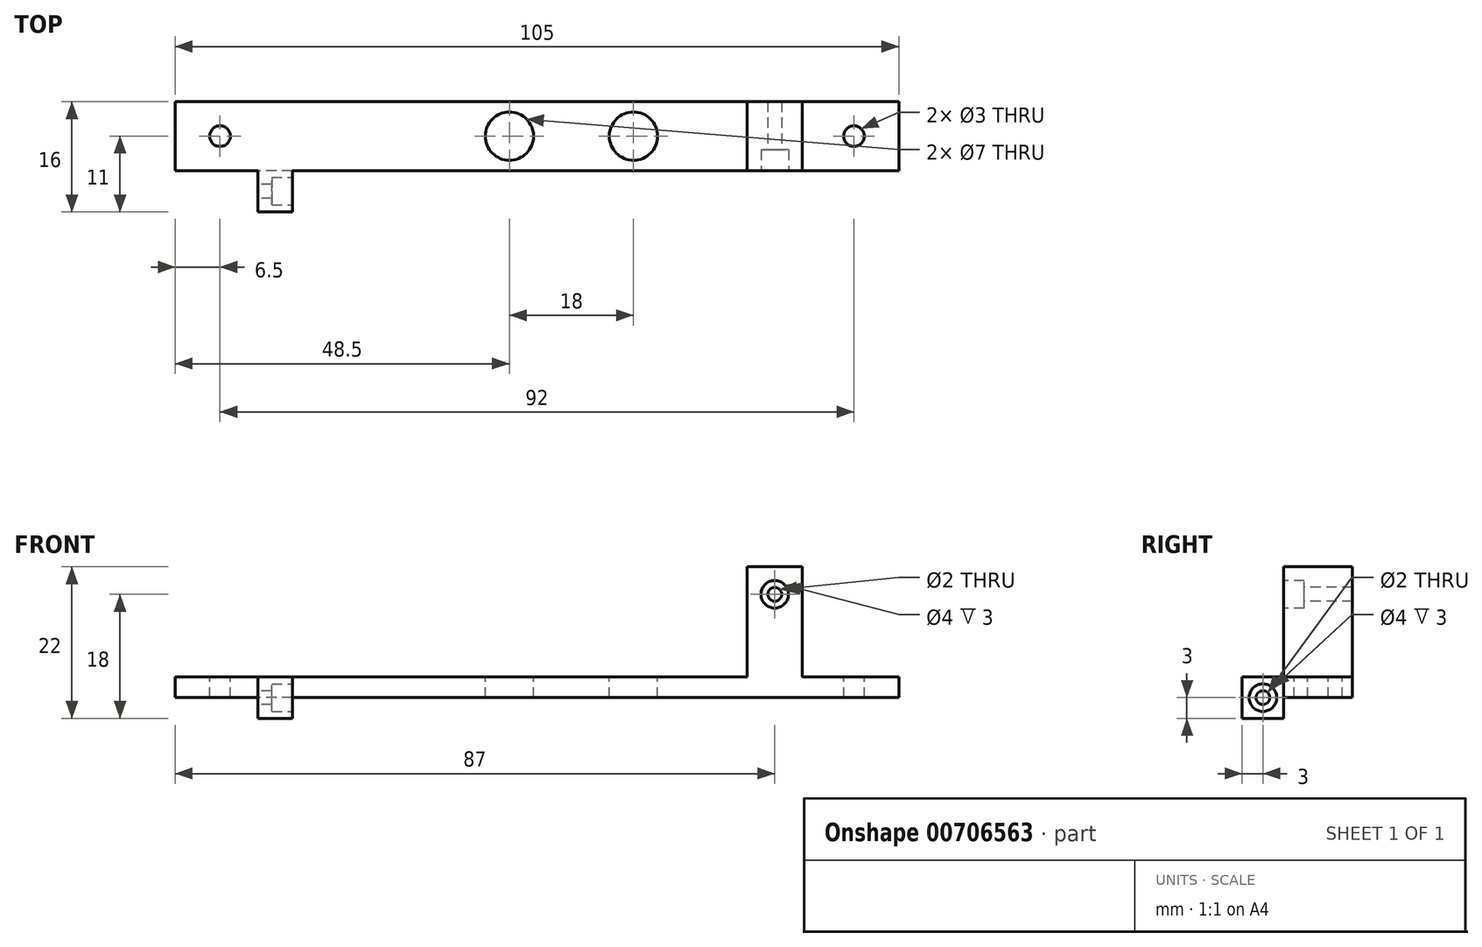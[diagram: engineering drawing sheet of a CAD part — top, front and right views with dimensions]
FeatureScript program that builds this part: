
annotation { "Feature Type Name" : "Feature", "Feature Type Description" : "" }
export const myFeature = defineFeature(function(context is Context, id is Id, definition is map)
    precondition{}
    {
        {
            var Q0;
            Q0=qCreatedBy(makeId("Top.planeOp"),FACE);
            var sketch = newSketch(context, id + "F0", { "sketchPlane" : qUnion([Q0])});
            skLineSegment(sketch, "E0.bottom", {"start": v(52.5, -5) * mm, "end": v(-52.5, -5) * mm});
            skLineSegment(sketch, "E0.top", {"start": v(52.5, 5) * mm, "end": v(-52.5, 5) * mm});
            skLineSegment(sketch, "E0.left", {"start": v(52.5, -5) * mm, "end": v(52.5, 5) * mm});
            skLineSegment(sketch, "E0.right", {"start": v(-52.5, -5) * mm, "end": v(-52.5, 5) * mm});
            skPoint(sketch, "E0.middle", {"position": v(0, 0) * mm});
            skLineSegment(sketch, "E1", {"start": v(-52.5, 0) * mm, "end": v(52.5, 0) * mm});
            skPoint(sketch, "E2", {"position": v(-46, 0) * mm});
            skPoint(sketch, "E3", {"position": v(46, 0) * mm});
            skSolve(sketch);
        }
        {
            var Q0;
            Q0 = qSketchRegion(id + "F0", true);
            extrude(context, id + "F1", {"entities" : qUnion([Q0]), "depth" : 3 * mm, "offsetDistance" : 25 * mm});
        }
        {
            var Q0;
            Q0=makeQuery(id+"F1.opExtrude","CAP_FACE",FACE,{"disambiguationData":[OSD([sQuery(id+"F0.wireOp",EDGE,"E0.bottom"),sQuery(id+"F0.wireOp",EDGE,"E0.top"),sQuery(id+"F0.wireOp",EDGE,"E0.left"),sQuery(id+"F0.wireOp",EDGE,"E0.right")])],"isStart":false});
            var sketch = newSketch(context, id + "F2", { "sketchPlane" : qUnion([Q0])});
            skLineSegment(sketch, "E4", {"start": v(-52.5, 0) * mm, "end": v(52.5, 0) * mm});
            skPoint(sketch, "E5", {"position": v(-46, 0) * mm});
            skPoint(sketch, "E6", {"position": v(46, 0) * mm});
            skCircle(sketch, "E7", {"center": v(-46, 0) * mm, "radius": 1.5 * mm});
            skCircle(sketch, "E8", {"center": v(46, 0) * mm, "radius": 1.5 * mm});
            skSolve(sketch);
        }
        {
            var Q0;
            Q0 = qSketchRegion(id + "F2", true);
            extrude(context, id + "F3", {"entities" : qUnion([Q0]), "operationType" : NewBodyOperationType.REMOVE, "endBound" : BoundingType.THROUGH_ALL, "oppositeDirection" : true, "depth" : 25 * mm, "offsetDistance" : 25 * mm});
        }
        {
            var Q0;
            Q0=makeQuery(id+"F1.opExtrude","CAP_FACE",FACE,{"disambiguationData":[OSD([sQuery(id+"F0.wireOp",EDGE,"E0.bottom"),sQuery(id+"F0.wireOp",EDGE,"E0.top"),sQuery(id+"F0.wireOp",EDGE,"E0.left"),sQuery(id+"F0.wireOp",EDGE,"E0.right")])],"isStart":false});
            var sketch = newSketch(context, id + "F4", { "sketchPlane" : qUnion([Q0])});
            skPoint(sketch, "E9", {"position": v(-4, 0) * mm});
            skPoint(sketch, "E10", {"position": v(14, 0) * mm});
            skPoint(sketch, "E11", {"position": v(-46, 0) * mm});
            skPoint(sketch, "E12", {"position": v(46, 0) * mm});
            skCircle(sketch, "E13", {"center": v(-4, 0) * mm, "radius": 3.5 * mm});
            skCircle(sketch, "E14", {"center": v(14, 0) * mm, "radius": 3.5 * mm});
            skSolve(sketch);
        }
        {
            var Q0;
            Q0 = qSketchRegion(id + "F4", true);
            extrude(context, id + "F5", {"entities" : qUnion([Q0]), "operationType" : NewBodyOperationType.REMOVE, "endBound" : BoundingType.THROUGH_ALL, "oppositeDirection" : true, "depth" : 25 * mm, "offsetDistance" : 25 * mm});
        }
        {
            var Q0;
            Q0 = qSketchRegion(id + "F4", true);
            extrude(context, id + "F6", {"entities" : qUnion([Q0]), "operationType" : NewBodyOperationType.REMOVE, "endBound" : BoundingType.THROUGH_ALL, "oppositeDirection" : true, "depth" : 25 * mm, "offsetDistance" : 25 * mm});
        }
        {
            var Q0;
            Q0=makeQuery(id+"F1.opExtrude","CAP_FACE",FACE,{"disambiguationData":[OSD([sQuery(id+"F0.wireOp",EDGE,"E0.bottom"),sQuery(id+"F0.wireOp",EDGE,"E0.top"),sQuery(id+"F0.wireOp",EDGE,"E0.left"),sQuery(id+"F0.wireOp",EDGE,"E0.right")])],"isStart":false});
            var sketch = newSketch(context, id + "F7", { "sketchPlane" : qUnion([Q0])});
            skPoint(sketch, "E15", {"position": v(38.5, -5) * mm});
            skLineSegment(sketch, "E16.bottom", {"start": v(38.5, -5) * mm, "end": v(30.5, -5) * mm});
            skLineSegment(sketch, "E16.top", {"start": v(38.5, 5) * mm, "end": v(30.5, 5) * mm});
            skLineSegment(sketch, "E16.left", {"start": v(38.5, -5) * mm, "end": v(38.5, 5) * mm});
            skLineSegment(sketch, "E16.right", {"start": v(30.5, -5) * mm, "end": v(30.5, 5) * mm});
            skSolve(sketch);
        }
        {
            var Q0;
            Q0 = qSketchRegion(id + "F7", true);
            extrude(context, id + "F8", {"entities" : qUnion([Q0]), "operationType" : NewBodyOperationType.ADD, "depth" : 16 * mm, "offsetDistance" : 25 * mm});
        }
        {
            var Q0;
            Q0=makeQuery(id+"F8.boolean.opBoolean","MERGE",FACE,{"derivedFrom":[makeQuery(id+"F1.opExtrude","SWEPT_FACE",FACE,{"disambiguationData":[OSD([sQuery(id+"F0.wireOp",EDGE,"E0.bottom")])]}),makeQuery(id+"F8.opExtrude","SWEPT_FACE",FACE,{"disambiguationData":[OSD([sQuery(id+"F7.wireOp",EDGE,"E16.bottom")])]})]});
            var sketch = newSketch(context, id + "F9", { "sketchPlane" : qUnion([Q0])});
            skPoint(sketch, "E17", {"position": v(34.5, 15) * mm});
            skCircle(sketch, "E18", {"center": v(34.5, 15) * mm, "radius": 1 * mm});
            skSolve(sketch);
        }
        {
            var Q0;
            Q0 = qSketchRegion(id + "F9", true);
            extrude(context, id + "F10", {"entities" : qUnion([Q0]), "operationType" : NewBodyOperationType.REMOVE, "endBound" : BoundingType.THROUGH_ALL, "oppositeDirection" : true, "depth" : 25 * mm, "offsetDistance" : 25 * mm});
        }
        {
            var Q0;
            Q0=makeQuery(id+"F8.boolean.opBoolean","MERGE",FACE,{"derivedFrom":[makeQuery(id+"F1.opExtrude","SWEPT_FACE",FACE,{"disambiguationData":[OSD([sQuery(id+"F0.wireOp",EDGE,"E0.bottom")])]}),makeQuery(id+"F8.opExtrude","SWEPT_FACE",FACE,{"disambiguationData":[OSD([sQuery(id+"F7.wireOp",EDGE,"E16.bottom")])]})]});
            var sketch = newSketch(context, id + "F11", { "sketchPlane" : qUnion([Q0])});
            skPoint(sketch, "E19", {"position": v(34.5, 15) * mm});
            skCircle(sketch, "E20", {"center": v(34.5, 15) * mm, "radius": 2 * mm});
            skSolve(sketch);
        }
        {
            var Q0;
            Q0 = qSketchRegion(id + "F11", true);
            extrude(context, id + "F12", {"entities" : qUnion([Q0]), "operationType" : NewBodyOperationType.REMOVE, "oppositeDirection" : true, "depth" : 3 * mm, "offsetDistance" : 25 * mm});
        }
        {
            var Q0;
            {var subQ0=sQuery(id+"F0.wireOp",EDGE,"E0.right");var subQ1=sQuery(id+"F0.wireOp",EDGE,"E0.top");var subQ2=sQuery(id+"F0.wireOp",EDGE,"E0.bottom");Q0=makeQuery(id+"F8.boolean.opBoolean","SPLIT",FACE,{"disambiguationData":[TD([makeQuery(id+"F1.opExtrude","SWEPT_FACE",FACE,{"disambiguationData":[OSD([subQ0])]})])],"derivedFrom":makeQuery(id+"F1.opExtrude","CAP_FACE",FACE,{"disambiguationData":[OSD([subQ2,subQ1,sQuery(id+"F0.wireOp",EDGE,"E0.left"),subQ0])],"isStart":false})});}
            var sketch = newSketch(context, id + "F13", { "sketchPlane" : qUnion([Q0])});
            skPoint(sketch, "E21", {"position": v(-40.5, -5) * mm});
            skLineSegment(sketch, "E22.bottom", {"start": v(-40.5, -5) * mm, "end": v(-35.5, -5) * mm});
            skLineSegment(sketch, "E22.top", {"start": v(-40.5, -11) * mm, "end": v(-35.5, -11) * mm});
            skLineSegment(sketch, "E22.left", {"start": v(-40.5, -5) * mm, "end": v(-40.5, -11) * mm});
            skLineSegment(sketch, "E22.right", {"start": v(-35.5, -5) * mm, "end": v(-35.5, -11) * mm});
            skSolve(sketch);
        }
        {
            var Q0;
            Q0 = qSketchRegion(id + "F13", true);
            extrude(context, id + "F14", {"entities" : qUnion([Q0]), "operationType" : NewBodyOperationType.ADD, "oppositeDirection" : true, "depth" : 6 * mm, "offsetDistance" : 25 * mm});
        }
        {
            var Q0;
            Q0=makeQuery(id+"F14.opExtrude","SWEPT_FACE",FACE,{"disambiguationData":[OSD([sQuery(id+"F13.wireOp",EDGE,"E22.left")])]});
            var sketch = newSketch(context, id + "F15", { "sketchPlane" : qUnion([Q0])});
            skPoint(sketch, "E23", {"position": v(8, 0) * mm});
            skPoint(sketch, "E23.positionSnap0", {"position": v(11, 0) * mm});
            skCircle(sketch, "E24", {"center": v(8, 0) * mm, "radius": 1 * mm});
            skSolve(sketch);
        }
        {
            var Q0;
            Q0 = qSketchRegion(id + "F15", true);
            extrude(context, id + "F16", {"entities" : qUnion([Q0]), "operationType" : NewBodyOperationType.REMOVE, "endBound" : BoundingType.THROUGH_ALL, "oppositeDirection" : true, "depth" : 25 * mm, "offsetDistance" : 25 * mm});
        }
        {
            var Q0;
            Q0=makeQuery(id+"F14.opExtrude","SWEPT_FACE",FACE,{"disambiguationData":[OSD([sQuery(id+"F13.wireOp",EDGE,"E22.right")])]});
            var sketch = newSketch(context, id + "F17", { "sketchPlane" : qUnion([Q0])});
            skPoint(sketch, "E25", {"position": v(-8, 0) * mm});
            skCircle(sketch, "E26", {"center": v(-8, 0) * mm, "radius": 2 * mm});
            skSolve(sketch);
        }
        {
            var Q0;
            Q0 = qSketchRegion(id + "F17", true);
            extrude(context, id + "F18", {"entities" : qUnion([Q0]), "operationType" : NewBodyOperationType.REMOVE, "oppositeDirection" : true, "depth" : 3 * mm, "offsetDistance" : 25 * mm});
        }
    });
